# Revit family: Rohrschelle Titan HD, M12, Gummi
name_source: partatom
category: HLS-Bauteile
revit_build: Autodesk Revit 2017 (Build: 20190507_1515(x64)
units: mm (PartAtom-declared; Revit-internal decimal feet)

## family parameters
Arbeitsebenenbasiert = Ja
Beim Laden mit Abzugskörper schneiden = Nein
Bemaßung runder Anschluss = Durchmesser verwenden
Gemeinsam genutzt = Ja
Immer vertikal = Nein
Raumberechnungspunkt = Nein
Teiletyp = Normal

## types (30) — shared parameters
A = 22 mm  [stored 0.0721785 ft]
Anschluss = M12
Anschlußhöhe = 22 mm
Bauart = zweiteilig
Baustoffklasse = B2
Brandschutz = RAL GZ 656
DF1 = 29 mm  [stored 0.0951444 ft]
DS = 6 mm  [stored 0.019685 ft]
DVS = 13 mm
Dämmstärke = 6 mm  [stored 0.019685 ft]
Fabrikat = MEFA
Farbe Schalldämmeinlage = schwarz
Firma = MEFA Befestigungs- und Montagesysteme GmbH
HGA = 11 mm  [stored 0.0360892 ft]
Kurztext1 = Rohrschelle Titan HD 50x5,0
MB = 50 mm  [stored 0.164042 ft]
MD = 5 mm  [stored 0.0164042 ft]
Material = Stahl
Material Schalldämmeinlage = TPE
Materialmaße = 50x5,0 mm
Materialname = S235
Mengeneinheit = St
Oberflaeche = galvanisch verzinkt
Schalldämmeinlage = Gummi
Verschluss = Schraubverschluss
Verschluss-Schraube = M12
Vorgabe-Ansicht = 1219 mm
max. Temperaturbeständigkeit = 100 °C
max. zul. Last horizontal = 0.00 kN
max. zul. Last vertikal = 0.00 kN
vpe = 1 St
zero-valued in all types: Nennweite DN Rohr, Stärke Material, max. Rohraußendurchmesser, min. Rohraußendurchmesser

## per-type parameters (varying)
| type | Achsabstand | Artikelnummer | B | Breite | D | D0 | DF2 | EAN | Gewicht | Gewicht pro Bauteil | H | Höhe | Kurztext2 | R | RM | Rohraußendurchmesser | Rohraußendurchmesser Zoll | S | max. Höhe | max. zul. Last |
| Titan HD, M12, Ø 64, Gummi | 125 mm | 0066504 | 154 mm | 154 mm | 64 mm  [stored 0.209974 ft] | 76 mm  [stored 0.249344 ft] | 13 mm | 4250928401557 | 0.92 kg | 0.92 kg | 97 mm | 97 mm | 64 mm M12 TPE | 38 mm  [stored 0.124672 ft] | 43 mm | 64 mm  [stored 0.209974 ft] | Zoll | 125 mm | 97 mm | 3.20 kN |
| Titan HD, M12, Ø 76, Gummi | 137 mm | 0066508 | 166 mm | 166 mm | 76 mm  [stored 0.249344 ft] | 88 mm  [stored 0.288714 ft] | 13 mm | 4250928401571 | 1.01 kg | 1.01 kg | 109 mm | 109 mm | 76 mm M12 TPE | 44 mm  [stored 0.144357 ft] | 49 mm | 76 mm  [stored 0.249344 ft] | 2 1/2 Zoll | 137 mm | 109 mm | 3.20 kN |
| Titan HD, M12, Ø 89, Gummi | 137 mm | 0066510 | 179 mm | 166 mm | 89 mm  [stored 0.291995 ft] | 101 mm | 13 mm | 4250928401571 | 1.01 kg | 1.01 kg | 122 mm | 109 mm | 76 mm M12 TPE | 51 mm | 56 mm | 76 mm  [stored 0.249344 ft] | 2 1/2 Zoll | 150 mm | 109 mm | 3.20 kN |
| Titan HD, M12, Ø108, Gummi | 170 mm | 0066516 | 198 mm | 199 mm | 108 mm | 120 mm | 13 mm | 4250928401618 | 1.25 kg | 1.25 kg | 141 mm | 141 mm | 108 mm M12 TPE | 60 mm  [stored 0.19685 ft] | 65 mm | 108 mm | Zoll | 169 mm | 141 mm | 3.20 kN |
| Titan HD, M12, Ø110, Gummi | 172 mm | 0066532 | 200 mm | 201 mm | 110 mm | 122 mm | 13 mm | 4250928401649 | 1.26 kg | 1.26 kg | 143 mm | 143 mm | 110 mm M12 TPE | 61 mm  [stored 0.200131 ft] | 66 mm | 110 mm | Zoll | 171 mm | 143 mm | 3.20 kN |
| Titan HD, M12, Ø133, Gummi | 195 mm | 0066605 | 224 mm | 224 mm | 133 mm | 145 mm | 14 mm  [stored 0.0459318 ft] | 4250928401700 | 1.44 kg | 1.44 kg | 166 mm | 166 mm | 133 mm M12 TPE | 73 mm | 78 mm | 133 mm | Zoll | 195 mm | 166 mm | 3.20 kN |
| Titan HD, M12, Ø135, Gummi | 197 mm | 0066613 | 226 mm | 226 mm | 135 mm | 147 mm | 14 mm  [stored 0.0459318 ft] | 4250928401724 | 1.45 kg | 1.45 kg | 168 mm | 168 mm | 135 mm M12 TPE | 74 mm | 79 mm | 135 mm | Zoll | 197 mm | 168 mm | 3.20 kN |
| Titan HD, M12, Ø140, Gummi | 202 mm | 0066621 | 231 mm | 231 mm | 140 mm | 152 mm | 14 mm  [stored 0.0459318 ft] | 4250928401731 | 1.49 kg | 1.49 kg | 173 mm | 173 mm | 140 mm M12 TPE | 76 mm  [stored 0.249344 ft] | 81 mm  [stored 0.265748 ft] | 140 mm | 5 Zoll | 202 mm | 173 mm | 3.20 kN |
| Titan HD, M12, Ø160, Gummi | 222 mm | 0066680 | 251 mm | 251 mm | 160 mm | 172 mm | 14 mm  [stored 0.0459318 ft] | 4250928401762 | 1.64 kg | 1.64 kg | 193 mm | 193 mm | 160 mm M12 TPE | 86 mm  [stored 0.282152 ft] | 91 mm  [stored 0.298556 ft] | 160 mm | Zoll | 222 mm | 193 mm | 3.20 kN |
| Titan HD, M12, Ø165, Gummi | 227 mm | 0066699 | 256 mm | 256 mm | 165 mm | 177 mm | 14 mm  [stored 0.0459318 ft] | 4250928401793 | 1.68 kg | 1.68 kg | 198 mm | 198 mm | 165 mm M12 TPE | 89 mm  [stored 0.291995 ft] | 94 mm | 165 mm | 6 Zoll | 227 mm | 198 mm | 3.20 kN |
| Titan HD, M12, Ø168, Gummi | 230 mm | 0066710 | 259 mm | 259 mm | 168 mm | 180 mm | 14 mm  [stored 0.0459318 ft] | 4250928401809 | 1.70 kg | 1.70 kg | 201 mm | 201 mm | 168 mm M12 TPE | 90 mm | 95 mm | 168 mm | Zoll | 230 mm | 201 mm | 3.20 kN |
| Titan HD, M12, Ø194, Gummi | 257 mm | 0066761 | 285 mm | 286 mm | 194 mm | 206 mm | 14 mm  [stored 0.0459318 ft] | 4250928401847 | 1.89 kg | 1.89 kg | 227 mm | 227 mm | 194 mm M12 TPE | 103 mm | 108 mm | 194 mm | Zoll | 256 mm | 227 mm | 11.50 kN |
| Titan HD, M12, Ø200, Gummi | 263 mm | 0066788 | 291 mm | 292 mm | 200 mm | 212 mm | 14 mm  [stored 0.0459318 ft] | 4250928401861 | 1.94 kg | 1.94 kg | 233 mm | 233 mm | 200 mm M12 TPE | 106 mm | 111 mm | 200 mm | Zoll | 262 mm | 233 mm | 11.50 kN |
| Titan HD, M12, Ø210, Gummi | 273 mm | 0066818 | 302 mm | 302 mm | 210 mm | 222 mm | 14 mm  [stored 0.0459318 ft] | 4250928401885 | 2.01 kg | 2.01 kg | 243 mm | 243 mm | 210 mm M12 TPE | 111 mm | 116 mm | 210 mm | Zoll | 273 mm | 243 mm | 11.50 kN |
| Titan HD, M12, Ø219, Gummi | 282 mm | 0066826 | 311 mm | 311 mm | 219 mm | 231 mm | 14 mm  [stored 0.0459318 ft] | 4250928401908 | 2.08 kg | 2.08 kg | 252 mm | 252 mm | 219 mm M12 TPE | 116 mm | 121 mm | 219 mm | 8 Zoll | 282 mm | 252 mm | 11.50 kN |
| Titan HD, M12, Ø267, Gummi | 330 mm | 0066893 | 359 mm | 359 mm | 267 mm | 279 mm | 14 mm  [stored 0.0459318 ft] | 4250928401946 | 2.44 kg | 2.44 kg | 300 mm | 300 mm | 267 mm M12 TPE | 140 mm | 145 mm | 267 mm | Zoll | 330 mm | 300 mm | 11.50 kN |
| Titan HD, M12, Ø273, Gummi | 336 mm | 0066907 | 365 mm | 365 mm | 273 mm | 285 mm | 14 mm  [stored 0.0459318 ft] | 4250928401960 | 2.49 kg | 2.49 kg | 306 mm | 306 mm | 273 mm M12 TPE | 143 mm | 148 mm | 273 mm | 10 Zoll | 336 mm | 306 mm | 11.50 kN |
| Titan HD, M12, Ø324, Gummi | 361 mm | 0066958 | 416 mm | 390 mm | 324 mm | 336 mm | 14 mm  [stored 0.0459318 ft] | 4250928401984 | 2.67 kg | 2.67 kg | 357 mm | 331 mm | 298 mm M12 TPE | 168 mm | 173 mm | 298 mm | Zoll | 387 mm | 331 mm | 11.50 kN |
| Titan HD, M12, Ø356, Gummi | 419 mm | 0066966 | 448 mm | 448 mm | 356 mm | 368 mm | 14 mm  [stored 0.0459318 ft] | 4250928402028 | 3.11 kg | 3.11 kg | 389 mm | 389 mm | 356 mm M12 TPE | 184 mm | 189 mm | 356 mm | Zoll | 419 mm | 389 mm | 11.50 kN |
| Titan HD, M12, Ø368, Gummi | 431 mm | 0066982 | 460 mm | 460 mm | 368 mm | 380 mm | 14 mm  [stored 0.0459318 ft] | 4250928402042 | 3.20 kg | 3.20 kg | 401 mm | 401 mm | 368 mm M12 TPE | 190 mm | 195 mm | 368 mm | Zoll | 431 mm | 401 mm | 11.50 kN |
| Titan HD, M12, Ø125, Gummi | 187 mm | 0066583 | 216 mm | 216 mm | 125 mm | 137 mm | 14 mm  [stored 0.0459318 ft] | 4250928401670 | 1.38 kg | 1.38 kg | 158 mm | 158 mm | 125 mm M12 TPE | 69 mm | 74 mm | 125 mm | Zoll | 187 mm | 158 mm | 3.20 kN |
| Titan HD, M12, Ø114, Gummi | 176 mm | 0066559 | 205 mm | 205 mm | 114 mm | 126 mm | 14 mm  [stored 0.0459318 ft] | 4250928401656 | 1.29 kg | 1.29 kg | 147 mm | 147 mm | 114 mm M12 TPE | 63 mm  [stored 0.206693 ft] | 68 mm  [stored 0.223097 ft] | 114 mm | 4 Zoll | 176 mm | 147 mm | 3.20 kN |
| Titan HD, M12, Ø127, Gummi | 189 mm | 0066591 | 218 mm | 218 mm | 127 mm | 139 mm | 14 mm  [stored 0.0459318 ft] | 4250928401687 | 1.39 kg | 1.39 kg | 160 mm | 160 mm | 127 mm M12 TPE | 70 mm | 75 mm | 127 mm | Zoll | 189 mm | 160 mm | 3.20 kN |
| Titan HD, M12, Ø152, Gummi | 214 mm | 0066648 | 243 mm | 243 mm | 152 mm | 164 mm | 14 mm  [stored 0.0459318 ft] | 4250928401748 | 1.58 kg | 1.58 kg | 185 mm | 185 mm | 152 mm M12 TPE | 82 mm  [stored 0.269029 ft] | 87 mm  [stored 0.285433 ft] | 152 mm | Zoll | 214 mm | 185 mm | 3.20 kN |
| Titan HD, M12, Ø177, Gummi | 239 mm | 0066737 | 268 mm | 268 mm | 177 mm | 189 mm | 14 mm  [stored 0.0459318 ft] | 4250928401816 | 1.77 kg | 1.77 kg | 210 mm | 210 mm | 177 mm M12 TPE | 95 mm | 100 mm | 177 mm | Zoll | 239 mm | 210 mm | 11.50 kN |
| Titan HD, M12, Ø180, Gummi | 242 mm | 0066753 | 271 mm | 271 mm | 180 mm | 192 mm | 14 mm  [stored 0.0459318 ft] | 4250928401823 | 1.79 kg | 1.79 kg | 213 mm | 213 mm | 180 mm M12 TPE | 96 mm | 101 mm | 180 mm | Zoll | 242 mm | 213 mm | 11.50 kN |
| Titan HD, M12, Ø225, Gummi | 288 mm | 0066842 | 317 mm | 317 mm | 225 mm | 237 mm | 14 mm  [stored 0.0459318 ft] | 4250928401915 | 2.13 kg | 2.13 kg | 258 mm | 258 mm | 225 mm M12 TPE | 119 mm | 124 mm | 225 mm | Zoll | 288 mm | 258 mm | 11.50 kN |
| Titan HD, M12, Ø245, Gummi | 308 mm | 0066877 | 337 mm | 337 mm | 245 mm | 257 mm | 14 mm  [stored 0.0459318 ft] | 4250928401922 | 2.28 kg | 2.28 kg | 278 mm | 278 mm | 245 mm M12 TPE | 129 mm | 134 mm | 245 mm | Zoll | 308 mm | 278 mm | 11.50 kN |
| Titan HD, M12, Ø280, Gummi | 343 mm | 0066923 | 372 mm | 372 mm | 280 mm | 292 mm | 14 mm  [stored 0.0459318 ft] | 4250928401977 | 2.54 kg | 2.54 kg | 313 mm | 313 mm | 280 mm M12 TPE | 146 mm | 151 mm | 280 mm | Zoll | 343 mm | 313 mm | 11.50 kN |
| Titan HD, M12, Ø298, Gummi | 361 mm | 0066931 | 390 mm | 390 mm | 298 mm | 310 mm | 14 mm  [stored 0.0459318 ft] | 4250928401984 | 2.67 kg | 2.67 kg | 331 mm | 331 mm | 298 mm M12 TPE | 155 mm | 160 mm | 298 mm | Zoll | 361 mm | 331 mm | 11.50 kN |

note: [stored X ft] marks values corroborated as IEEE doubles in the binary element streams (Revit-internal decimal feet)

## geometry (parser evidence)
native form markers: Sweep x5
no freeform markers — native parametric forms only
